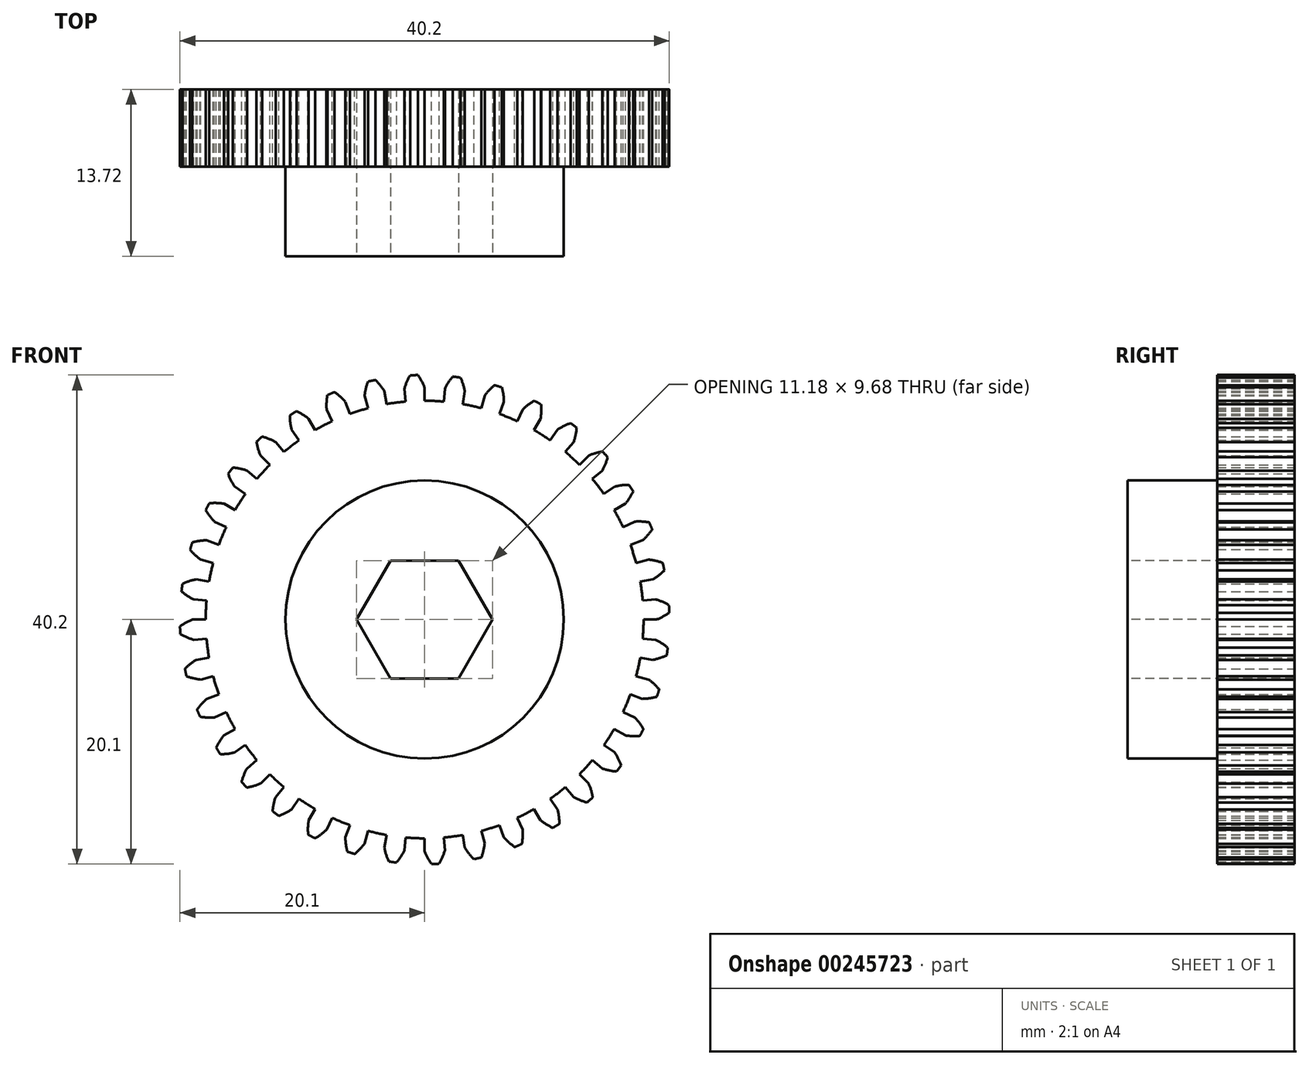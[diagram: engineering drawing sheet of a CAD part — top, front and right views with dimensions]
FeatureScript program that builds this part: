
annotation { "Feature Type Name" : "Feature", "Feature Type Description" : "" }
export const myFeature = defineFeature(function(context is Context, id is Id, definition is map)
    precondition{}
    {
        {
            var Q0;
            Q0=qCreatedBy(makeId("Front.planeOp"),FACE);
            var sketch = newSketch(context, id + "F0", { "sketchPlane" : qUnion([Q0])});
            skArc(sketch, "E0", {"start": v(4.65, 17.37) * mm, "mid": v(-6.88, -16.61) * mm, "end": v(9, 15.57) * mm});
            skLineSegment(sketch, "E1", {"start": v(0, 17.98) * mm, "end": v(0, 19.05) * mm});
            skLineSegment(sketch, "E2", {"start": v(0, 0) * mm, "end": v(-0.88, 20.08) * mm, "construction": true});
            skArc(sketch, "E3.trimOffspring", {"start": v(-0.56, 20.1) * mm, "mid": v(-0.72, 20.1) * mm, "end": v(-0.88, 20.08) * mm});
            skArc(sketch, "E4.trimOffspring", {"start": v(0, 19.05) * mm, "mid": v(-0.25, 19.6) * mm, "end": v(-0.56, 20.1) * mm});
            skLineSegment(sketch, "E5.MirrorCS", {"start": v(-1.57, 17.91) * mm, "end": v(-1.66, 18.98) * mm});
            skArc(sketch, "E6.MirrorCS", {"start": v(-1.66, 18.98) * mm, "mid": v(-1.46, 19.54) * mm, "end": v(-1.2, 20.07) * mm});
            skArc(sketch, "E7.MirrorCS", {"start": v(-1.2, 20.07) * mm, "mid": v(-1.03, 20.08) * mm, "end": v(-0.88, 20.08) * mm});
            skLineSegment(sketch, "E8.1.0", {"start": v(-4.65, 17.37) * mm, "end": v(-4.93, 18.4) * mm});
            skArc(sketch, "E8.1.1", {"start": v(-3.3, 18.76) * mm, "mid": v(-3.65, 19.25) * mm, "end": v(-4.04, 19.7) * mm});
            skLineSegment(sketch, "E8.1.2", {"start": v(-3.12, 17.7) * mm, "end": v(-3.3, 18.76) * mm});
            skArc(sketch, "E8.1.3", {"start": v(-4.93, 18.4) * mm, "mid": v(-4.83, 18.99) * mm, "end": v(-4.66, 19.56) * mm});
            skArc(sketch, "E8.1.4", {"start": v(-4.66, 19.56) * mm, "mid": v(-4.5, 19.6) * mm, "end": v(-4.35, 19.63) * mm});
            skArc(sketch, "E8.1.5", {"start": v(-4.04, 19.7) * mm, "mid": v(-4.2, 19.66) * mm, "end": v(-4.35, 19.63) * mm});
            skLineSegment(sketch, "E8.2.0", {"start": v(-7.6, 16.3) * mm, "end": v(-8.05, 17.27) * mm});
            skArc(sketch, "E8.2.1", {"start": v(-6.52, 17.9) * mm, "mid": v(-6.93, 18.32) * mm, "end": v(-7.4, 18.7) * mm});
            skLineSegment(sketch, "E8.2.2", {"start": v(-6.15, 16.9) * mm, "end": v(-6.52, 17.9) * mm});
            skArc(sketch, "E8.2.3", {"start": v(-8.05, 17.27) * mm, "mid": v(-8.05, 17.86) * mm, "end": v(-7.98, 18.45) * mm});
            skArc(sketch, "E8.2.4", {"start": v(-7.98, 18.45) * mm, "mid": v(-7.84, 18.51) * mm, "end": v(-7.7, 18.57) * mm});
            skArc(sketch, "E8.2.5", {"start": v(-7.4, 18.7) * mm, "mid": v(-7.55, 18.63) * mm, "end": v(-7.7, 18.57) * mm});
            skLineSegment(sketch, "E8.3.0", {"start": v(-10.31, 14.73) * mm, "end": v(-10.93, 15.6) * mm});
            skArc(sketch, "E8.3.1", {"start": v(-9.52, 16.5) * mm, "mid": v(-10, 16.84) * mm, "end": v(-10.53, 17.12) * mm});
            skLineSegment(sketch, "E8.3.2", {"start": v(-9, 15.57) * mm, "end": v(-9.52, 16.5) * mm});
            skArc(sketch, "E8.3.3", {"start": v(-10.93, 15.6) * mm, "mid": v(-11.03, 16.19) * mm, "end": v(-11.07, 16.78) * mm});
            skArc(sketch, "E8.3.4", {"start": v(-11.07, 16.78) * mm, "mid": v(-10.93, 16.87) * mm, "end": v(-10.8, 16.96) * mm});
            skArc(sketch, "E8.3.5", {"start": v(-10.53, 17.12) * mm, "mid": v(-10.67, 17.04) * mm, "end": v(-10.8, 16.96) * mm});
            skLineSegment(sketch, "E8.4.0", {"start": v(-12.72, 12.72) * mm, "end": v(-13.47, 13.47) * mm});
            skArc(sketch, "E8.4.1", {"start": v(-12.25, 14.6) * mm, "mid": v(-12.78, 14.85) * mm, "end": v(-13.35, 15.03) * mm});
            skLineSegment(sketch, "E8.4.2", {"start": v(-11.56, 13.78) * mm, "end": v(-12.25, 14.6) * mm});
            skArc(sketch, "E8.4.3", {"start": v(-13.47, 13.47) * mm, "mid": v(-13.68, 14.03) * mm, "end": v(-13.81, 14.6) * mm});
            skArc(sketch, "E8.4.4", {"start": v(-13.81, 14.6) * mm, "mid": v(-13.7, 14.72) * mm, "end": v(-13.58, 14.82) * mm});
            skArc(sketch, "E8.4.5", {"start": v(-13.35, 15.03) * mm, "mid": v(-13.47, 14.93) * mm, "end": v(-13.58, 14.82) * mm});
            skLineSegment(sketch, "E8.5.0", {"start": v(-14.73, 10.31) * mm, "end": v(-15.6, 10.93) * mm});
            skArc(sketch, "E8.5.1", {"start": v(-14.6, 12.25) * mm, "mid": v(-15.17, 12.4) * mm, "end": v(-15.76, 12.49) * mm});
            skLineSegment(sketch, "E8.5.2", {"start": v(-13.78, 11.56) * mm, "end": v(-14.6, 12.25) * mm});
            skArc(sketch, "E8.5.3", {"start": v(-15.6, 10.93) * mm, "mid": v(-15.9, 11.44) * mm, "end": v(-16.14, 11.99) * mm});
            skArc(sketch, "E8.5.4", {"start": v(-16.14, 11.99) * mm, "mid": v(-16.05, 12.11) * mm, "end": v(-15.95, 12.24) * mm});
            skArc(sketch, "E8.5.5", {"start": v(-15.76, 12.49) * mm, "mid": v(-15.85, 12.36) * mm, "end": v(-15.95, 12.24) * mm});
            skLineSegment(sketch, "E8.6.0", {"start": v(-16.3, 7.6) * mm, "end": v(-17.27, 8.05) * mm});
            skArc(sketch, "E8.6.1", {"start": v(-16.5, 9.53) * mm, "mid": v(-17.09, 9.58) * mm, "end": v(-17.68, 9.56) * mm});
            skLineSegment(sketch, "E8.6.2", {"start": v(-15.57, 9) * mm, "end": v(-16.5, 9.53) * mm});
            skArc(sketch, "E8.6.3", {"start": v(-17.27, 8.05) * mm, "mid": v(-17.65, 8.5) * mm, "end": v(-17.98, 9) * mm});
            skArc(sketch, "E8.6.4", {"start": v(-17.98, 9) * mm, "mid": v(-17.9, 9.14) * mm, "end": v(-17.83, 9.28) * mm});
            skArc(sketch, "E8.6.5", {"start": v(-17.68, 9.56) * mm, "mid": v(-17.76, 9.42) * mm, "end": v(-17.83, 9.28) * mm});
            skLineSegment(sketch, "E8.7.0", {"start": v(-17.37, 4.65) * mm, "end": v(-18.4, 4.93) * mm});
            skArc(sketch, "E8.7.1", {"start": v(-17.9, 6.52) * mm, "mid": v(-18.5, 6.47) * mm, "end": v(-19.08, 6.35) * mm});
            skLineSegment(sketch, "E8.7.2", {"start": v(-16.9, 6.15) * mm, "end": v(-17.9, 6.52) * mm});
            skArc(sketch, "E8.7.3", {"start": v(-18.4, 4.93) * mm, "mid": v(-18.86, 5.3) * mm, "end": v(-19.27, 5.74) * mm});
            skArc(sketch, "E8.7.4", {"start": v(-19.27, 5.74) * mm, "mid": v(-19.22, 5.9) * mm, "end": v(-19.17, 6.05) * mm});
            skArc(sketch, "E8.7.5", {"start": v(-19.08, 6.35) * mm, "mid": v(-19.13, 6.2) * mm, "end": v(-19.17, 6.05) * mm});
            skLineSegment(sketch, "E8.8.0", {"start": v(-17.91, 1.57) * mm, "end": v(-18.98, 1.66) * mm});
            skArc(sketch, "E8.8.1", {"start": v(-18.76, 3.3) * mm, "mid": v(-19.34, 3.16) * mm, "end": v(-19.89, 2.94) * mm});
            skLineSegment(sketch, "E8.8.2", {"start": v(-17.7, 3.12) * mm, "end": v(-18.76, 3.3) * mm});
            skArc(sketch, "E8.8.3", {"start": v(-18.98, 1.66) * mm, "mid": v(-19.5, 1.95) * mm, "end": v(-19.97, 2.31) * mm});
            skArc(sketch, "E8.8.4", {"start": v(-19.97, 2.31) * mm, "mid": v(-19.95, 2.47) * mm, "end": v(-19.93, 2.62) * mm});
            skArc(sketch, "E8.8.5", {"start": v(-19.89, 2.94) * mm, "mid": v(-19.91, 2.78) * mm, "end": v(-19.93, 2.62) * mm});
            skLineSegment(sketch, "E8.9.0", {"start": v(-17.91, -1.57) * mm, "end": v(-18.98, -1.66) * mm});
            skArc(sketch, "E8.9.1", {"start": v(-19.05, 0) * mm, "mid": v(-19.6, -0.25) * mm, "end": v(-20.1, -0.56) * mm});
            skLineSegment(sketch, "E8.9.2", {"start": v(-17.98, 0) * mm, "end": v(-19.05, 0) * mm});
            skArc(sketch, "E8.9.3", {"start": v(-18.98, -1.66) * mm, "mid": v(-19.54, -1.46) * mm, "end": v(-20.07, -1.2) * mm});
            skArc(sketch, "E8.9.4", {"start": v(-20.07, -1.2) * mm, "mid": v(-20.08, -1.03) * mm, "end": v(-20.08, -0.88) * mm});
            skArc(sketch, "E8.9.5", {"start": v(-20.1, -0.56) * mm, "mid": v(-20.1, -0.72) * mm, "end": v(-20.08, -0.88) * mm});
            skLineSegment(sketch, "E8.10.0", {"start": v(-17.37, -4.65) * mm, "end": v(-18.4, -4.93) * mm});
            skArc(sketch, "E8.10.1", {"start": v(-18.76, -3.3) * mm, "mid": v(-19.25, -3.65) * mm, "end": v(-19.7, -4.04) * mm});
            skLineSegment(sketch, "E8.10.2", {"start": v(-17.7, -3.12) * mm, "end": v(-18.76, -3.3) * mm});
            skArc(sketch, "E8.10.3", {"start": v(-18.4, -4.93) * mm, "mid": v(-18.99, -4.83) * mm, "end": v(-19.56, -4.66) * mm});
            skArc(sketch, "E8.10.4", {"start": v(-19.56, -4.66) * mm, "mid": v(-19.6, -4.5) * mm, "end": v(-19.63, -4.35) * mm});
            skArc(sketch, "E8.10.5", {"start": v(-19.7, -4.04) * mm, "mid": v(-19.66, -4.2) * mm, "end": v(-19.63, -4.35) * mm});
            skLineSegment(sketch, "E8.11.0", {"start": v(-16.3, -7.6) * mm, "end": v(-17.27, -8.05) * mm});
            skArc(sketch, "E8.11.1", {"start": v(-17.9, -6.52) * mm, "mid": v(-18.32, -6.93) * mm, "end": v(-18.7, -7.4) * mm});
            skLineSegment(sketch, "E8.11.2", {"start": v(-16.9, -6.15) * mm, "end": v(-17.9, -6.52) * mm});
            skArc(sketch, "E8.11.3", {"start": v(-17.27, -8.05) * mm, "mid": v(-17.86, -8.05) * mm, "end": v(-18.45, -7.98) * mm});
            skArc(sketch, "E8.11.4", {"start": v(-18.45, -7.98) * mm, "mid": v(-18.51, -7.84) * mm, "end": v(-18.57, -7.7) * mm});
            skArc(sketch, "E8.11.5", {"start": v(-18.7, -7.4) * mm, "mid": v(-18.63, -7.55) * mm, "end": v(-18.57, -7.7) * mm});
            skLineSegment(sketch, "E8.12.0", {"start": v(-14.73, -10.31) * mm, "end": v(-15.6, -10.93) * mm});
            skArc(sketch, "E8.12.1", {"start": v(-16.5, -9.52) * mm, "mid": v(-16.84, -10) * mm, "end": v(-17.12, -10.53) * mm});
            skLineSegment(sketch, "E8.12.2", {"start": v(-15.57, -9) * mm, "end": v(-16.5, -9.52) * mm});
            skArc(sketch, "E8.12.3", {"start": v(-15.6, -10.93) * mm, "mid": v(-16.19, -11.03) * mm, "end": v(-16.78, -11.07) * mm});
            skArc(sketch, "E8.12.4", {"start": v(-16.78, -11.07) * mm, "mid": v(-16.87, -10.93) * mm, "end": v(-16.96, -10.8) * mm});
            skArc(sketch, "E8.12.5", {"start": v(-17.12, -10.53) * mm, "mid": v(-17.04, -10.67) * mm, "end": v(-16.96, -10.8) * mm});
            skLineSegment(sketch, "E8.13.0", {"start": v(-12.72, -12.72) * mm, "end": v(-13.47, -13.47) * mm});
            skArc(sketch, "E8.13.1", {"start": v(-14.6, -12.25) * mm, "mid": v(-14.85, -12.78) * mm, "end": v(-15.03, -13.35) * mm});
            skLineSegment(sketch, "E8.13.2", {"start": v(-13.78, -11.56) * mm, "end": v(-14.6, -12.25) * mm});
            skArc(sketch, "E8.13.3", {"start": v(-13.47, -13.47) * mm, "mid": v(-14.03, -13.68) * mm, "end": v(-14.6, -13.81) * mm});
            skArc(sketch, "E8.13.4", {"start": v(-14.6, -13.81) * mm, "mid": v(-14.72, -13.7) * mm, "end": v(-14.82, -13.58) * mm});
            skArc(sketch, "E8.13.5", {"start": v(-15.03, -13.35) * mm, "mid": v(-14.93, -13.47) * mm, "end": v(-14.82, -13.58) * mm});
            skLineSegment(sketch, "E8.14.0", {"start": v(-10.31, -14.73) * mm, "end": v(-10.93, -15.6) * mm});
            skArc(sketch, "E8.14.1", {"start": v(-12.25, -14.6) * mm, "mid": v(-12.4, -15.17) * mm, "end": v(-12.49, -15.76) * mm});
            skLineSegment(sketch, "E8.14.2", {"start": v(-11.56, -13.78) * mm, "end": v(-12.25, -14.6) * mm});
            skArc(sketch, "E8.14.3", {"start": v(-10.93, -15.6) * mm, "mid": v(-11.44, -15.9) * mm, "end": v(-11.99, -16.14) * mm});
            skArc(sketch, "E8.14.4", {"start": v(-11.99, -16.14) * mm, "mid": v(-12.11, -16.05) * mm, "end": v(-12.24, -15.95) * mm});
            skArc(sketch, "E8.14.5", {"start": v(-12.49, -15.76) * mm, "mid": v(-12.36, -15.85) * mm, "end": v(-12.24, -15.95) * mm});
            skLineSegment(sketch, "E8.15.0", {"start": v(-7.6, -16.3) * mm, "end": v(-8.05, -17.27) * mm});
            skArc(sketch, "E8.15.1", {"start": v(-9.53, -16.5) * mm, "mid": v(-9.58, -17.09) * mm, "end": v(-9.56, -17.68) * mm});
            skLineSegment(sketch, "E8.15.2", {"start": v(-9, -15.57) * mm, "end": v(-9.53, -16.5) * mm});
            skArc(sketch, "E8.15.3", {"start": v(-8.05, -17.27) * mm, "mid": v(-8.5, -17.65) * mm, "end": v(-9, -17.98) * mm});
            skArc(sketch, "E8.15.4", {"start": v(-9, -17.98) * mm, "mid": v(-9.14, -17.9) * mm, "end": v(-9.28, -17.83) * mm});
            skArc(sketch, "E8.15.5", {"start": v(-9.56, -17.68) * mm, "mid": v(-9.42, -17.76) * mm, "end": v(-9.28, -17.83) * mm});
            skLineSegment(sketch, "E8.16.0", {"start": v(-4.65, -17.37) * mm, "end": v(-4.93, -18.4) * mm});
            skArc(sketch, "E8.16.1", {"start": v(-6.52, -17.9) * mm, "mid": v(-6.47, -18.5) * mm, "end": v(-6.35, -19.08) * mm});
            skLineSegment(sketch, "E8.16.2", {"start": v(-6.15, -16.9) * mm, "end": v(-6.52, -17.9) * mm});
            skArc(sketch, "E8.16.3", {"start": v(-4.93, -18.4) * mm, "mid": v(-5.3, -18.86) * mm, "end": v(-5.74, -19.27) * mm});
            skArc(sketch, "E8.16.4", {"start": v(-5.74, -19.27) * mm, "mid": v(-5.9, -19.22) * mm, "end": v(-6.05, -19.17) * mm});
            skArc(sketch, "E8.16.5", {"start": v(-6.35, -19.08) * mm, "mid": v(-6.2, -19.13) * mm, "end": v(-6.05, -19.17) * mm});
            skLineSegment(sketch, "E8.17.0", {"start": v(-1.57, -17.91) * mm, "end": v(-1.66, -18.98) * mm});
            skArc(sketch, "E8.17.1", {"start": v(-3.3, -18.76) * mm, "mid": v(-3.16, -19.34) * mm, "end": v(-2.94, -19.89) * mm});
            skLineSegment(sketch, "E8.17.2", {"start": v(-3.12, -17.7) * mm, "end": v(-3.3, -18.76) * mm});
            skArc(sketch, "E8.17.3", {"start": v(-1.66, -18.98) * mm, "mid": v(-1.95, -19.5) * mm, "end": v(-2.31, -19.97) * mm});
            skArc(sketch, "E8.17.4", {"start": v(-2.31, -19.97) * mm, "mid": v(-2.47, -19.95) * mm, "end": v(-2.62, -19.93) * mm});
            skArc(sketch, "E8.17.5", {"start": v(-2.94, -19.89) * mm, "mid": v(-2.78, -19.91) * mm, "end": v(-2.62, -19.93) * mm});
            skLineSegment(sketch, "E8.18.0", {"start": v(1.57, -17.91) * mm, "end": v(1.66, -18.98) * mm});
            skArc(sketch, "E8.18.1", {"start": v(0, -19.05) * mm, "mid": v(0.25, -19.6) * mm, "end": v(0.56, -20.1) * mm});
            skLineSegment(sketch, "E8.18.2", {"start": v(0, -17.98) * mm, "end": v(0, -19.05) * mm});
            skArc(sketch, "E8.18.3", {"start": v(1.66, -18.98) * mm, "mid": v(1.46, -19.54) * mm, "end": v(1.2, -20.07) * mm});
            skArc(sketch, "E8.18.4", {"start": v(1.2, -20.07) * mm, "mid": v(1.03, -20.08) * mm, "end": v(0.88, -20.08) * mm});
            skArc(sketch, "E8.18.5", {"start": v(0.56, -20.1) * mm, "mid": v(0.72, -20.1) * mm, "end": v(0.88, -20.08) * mm});
            skLineSegment(sketch, "E8.19.0", {"start": v(4.65, -17.37) * mm, "end": v(4.93, -18.4) * mm});
            skArc(sketch, "E8.19.1", {"start": v(3.3, -18.76) * mm, "mid": v(3.65, -19.25) * mm, "end": v(4.04, -19.7) * mm});
            skLineSegment(sketch, "E8.19.2", {"start": v(3.12, -17.7) * mm, "end": v(3.3, -18.76) * mm});
            skArc(sketch, "E8.19.3", {"start": v(4.93, -18.4) * mm, "mid": v(4.83, -18.99) * mm, "end": v(4.66, -19.56) * mm});
            skArc(sketch, "E8.19.4", {"start": v(4.66, -19.56) * mm, "mid": v(4.5, -19.6) * mm, "end": v(4.35, -19.63) * mm});
            skArc(sketch, "E8.19.5", {"start": v(4.04, -19.7) * mm, "mid": v(4.2, -19.66) * mm, "end": v(4.35, -19.63) * mm});
            skLineSegment(sketch, "E8.20.0", {"start": v(7.6, -16.3) * mm, "end": v(8.05, -17.27) * mm});
            skArc(sketch, "E8.20.1", {"start": v(6.52, -17.9) * mm, "mid": v(6.93, -18.32) * mm, "end": v(7.4, -18.7) * mm});
            skLineSegment(sketch, "E8.20.2", {"start": v(6.15, -16.9) * mm, "end": v(6.52, -17.9) * mm});
            skArc(sketch, "E8.20.3", {"start": v(8.05, -17.27) * mm, "mid": v(8.05, -17.86) * mm, "end": v(7.98, -18.45) * mm});
            skArc(sketch, "E8.20.4", {"start": v(7.98, -18.45) * mm, "mid": v(7.84, -18.51) * mm, "end": v(7.7, -18.57) * mm});
            skArc(sketch, "E8.20.5", {"start": v(7.4, -18.7) * mm, "mid": v(7.55, -18.63) * mm, "end": v(7.7, -18.57) * mm});
            skLineSegment(sketch, "E8.21.0", {"start": v(10.31, -14.73) * mm, "end": v(10.93, -15.6) * mm});
            skArc(sketch, "E8.21.1", {"start": v(9.52, -16.5) * mm, "mid": v(10, -16.84) * mm, "end": v(10.53, -17.12) * mm});
            skLineSegment(sketch, "E8.21.2", {"start": v(9, -15.57) * mm, "end": v(9.53, -16.5) * mm});
            skArc(sketch, "E8.21.3", {"start": v(10.93, -15.6) * mm, "mid": v(11.03, -16.19) * mm, "end": v(11.07, -16.78) * mm});
            skArc(sketch, "E8.21.4", {"start": v(11.07, -16.78) * mm, "mid": v(10.93, -16.87) * mm, "end": v(10.8, -16.96) * mm});
            skArc(sketch, "E8.21.5", {"start": v(10.53, -17.12) * mm, "mid": v(10.67, -17.04) * mm, "end": v(10.8, -16.96) * mm});
            skLineSegment(sketch, "E8.22.0", {"start": v(12.72, -12.72) * mm, "end": v(13.47, -13.47) * mm});
            skArc(sketch, "E8.22.1", {"start": v(12.25, -14.6) * mm, "mid": v(12.78, -14.85) * mm, "end": v(13.35, -15.03) * mm});
            skLineSegment(sketch, "E8.22.2", {"start": v(11.56, -13.78) * mm, "end": v(12.25, -14.6) * mm});
            skArc(sketch, "E8.22.3", {"start": v(13.47, -13.47) * mm, "mid": v(13.68, -14.03) * mm, "end": v(13.81, -14.6) * mm});
            skArc(sketch, "E8.22.4", {"start": v(13.81, -14.6) * mm, "mid": v(13.7, -14.72) * mm, "end": v(13.58, -14.82) * mm});
            skArc(sketch, "E8.22.5", {"start": v(13.35, -15.03) * mm, "mid": v(13.47, -14.93) * mm, "end": v(13.58, -14.82) * mm});
            skLineSegment(sketch, "E8.23.0", {"start": v(14.73, -10.31) * mm, "end": v(15.6, -10.93) * mm});
            skArc(sketch, "E8.23.1", {"start": v(14.6, -12.25) * mm, "mid": v(15.17, -12.4) * mm, "end": v(15.76, -12.49) * mm});
            skLineSegment(sketch, "E8.23.2", {"start": v(13.78, -11.56) * mm, "end": v(14.6, -12.25) * mm});
            skArc(sketch, "E8.23.3", {"start": v(15.6, -10.93) * mm, "mid": v(15.9, -11.44) * mm, "end": v(16.14, -11.99) * mm});
            skArc(sketch, "E8.23.4", {"start": v(16.14, -11.99) * mm, "mid": v(16.05, -12.11) * mm, "end": v(15.95, -12.24) * mm});
            skArc(sketch, "E8.23.5", {"start": v(15.76, -12.49) * mm, "mid": v(15.85, -12.36) * mm, "end": v(15.95, -12.24) * mm});
            skLineSegment(sketch, "E8.24.0", {"start": v(16.3, -7.6) * mm, "end": v(17.27, -8.05) * mm});
            skArc(sketch, "E8.24.1", {"start": v(16.5, -9.53) * mm, "mid": v(17.09, -9.58) * mm, "end": v(17.68, -9.56) * mm});
            skLineSegment(sketch, "E8.24.2", {"start": v(15.57, -9) * mm, "end": v(16.5, -9.53) * mm});
            skArc(sketch, "E8.24.3", {"start": v(17.27, -8.05) * mm, "mid": v(17.65, -8.5) * mm, "end": v(17.98, -9) * mm});
            skArc(sketch, "E8.24.4", {"start": v(17.98, -9) * mm, "mid": v(17.9, -9.14) * mm, "end": v(17.83, -9.28) * mm});
            skArc(sketch, "E8.24.5", {"start": v(17.68, -9.56) * mm, "mid": v(17.76, -9.42) * mm, "end": v(17.83, -9.28) * mm});
            skLineSegment(sketch, "E8.25.0", {"start": v(17.37, -4.65) * mm, "end": v(18.4, -4.93) * mm});
            skArc(sketch, "E8.25.1", {"start": v(17.9, -6.52) * mm, "mid": v(18.5, -6.47) * mm, "end": v(19.08, -6.35) * mm});
            skLineSegment(sketch, "E8.25.2", {"start": v(16.9, -6.15) * mm, "end": v(17.9, -6.52) * mm});
            skArc(sketch, "E8.25.3", {"start": v(18.4, -4.93) * mm, "mid": v(18.86, -5.3) * mm, "end": v(19.27, -5.74) * mm});
            skArc(sketch, "E8.25.4", {"start": v(19.27, -5.74) * mm, "mid": v(19.22, -5.9) * mm, "end": v(19.17, -6.05) * mm});
            skArc(sketch, "E8.25.5", {"start": v(19.08, -6.35) * mm, "mid": v(19.13, -6.2) * mm, "end": v(19.17, -6.05) * mm});
            skLineSegment(sketch, "E8.26.0", {"start": v(17.91, -1.57) * mm, "end": v(18.98, -1.66) * mm});
            skArc(sketch, "E8.26.1", {"start": v(18.76, -3.3) * mm, "mid": v(19.34, -3.16) * mm, "end": v(19.89, -2.94) * mm});
            skLineSegment(sketch, "E8.26.2", {"start": v(17.7, -3.12) * mm, "end": v(18.76, -3.3) * mm});
            skArc(sketch, "E8.26.3", {"start": v(18.98, -1.66) * mm, "mid": v(19.5, -1.95) * mm, "end": v(19.97, -2.31) * mm});
            skArc(sketch, "E8.26.4", {"start": v(19.97, -2.31) * mm, "mid": v(19.95, -2.47) * mm, "end": v(19.93, -2.62) * mm});
            skArc(sketch, "E8.26.5", {"start": v(19.89, -2.94) * mm, "mid": v(19.91, -2.78) * mm, "end": v(19.93, -2.62) * mm});
            skLineSegment(sketch, "E8.27.0", {"start": v(17.91, 1.57) * mm, "end": v(18.98, 1.66) * mm});
            skArc(sketch, "E8.27.1", {"start": v(19.05, 0) * mm, "mid": v(19.6, 0.25) * mm, "end": v(20.1, 0.56) * mm});
            skLineSegment(sketch, "E8.27.2", {"start": v(17.98, 0) * mm, "end": v(19.05, 0) * mm});
            skArc(sketch, "E8.27.3", {"start": v(18.98, 1.66) * mm, "mid": v(19.54, 1.46) * mm, "end": v(20.07, 1.2) * mm});
            skArc(sketch, "E8.27.4", {"start": v(20.07, 1.2) * mm, "mid": v(20.08, 1.03) * mm, "end": v(20.08, 0.88) * mm});
            skArc(sketch, "E8.27.5", {"start": v(20.1, 0.56) * mm, "mid": v(20.1, 0.72) * mm, "end": v(20.08, 0.88) * mm});
            skLineSegment(sketch, "E8.28.0", {"start": v(17.37, 4.65) * mm, "end": v(18.4, 4.93) * mm});
            skArc(sketch, "E8.28.1", {"start": v(18.76, 3.3) * mm, "mid": v(19.25, 3.65) * mm, "end": v(19.7, 4.04) * mm});
            skLineSegment(sketch, "E8.28.2", {"start": v(17.7, 3.12) * mm, "end": v(18.76, 3.3) * mm});
            skArc(sketch, "E8.28.3", {"start": v(18.4, 4.93) * mm, "mid": v(18.99, 4.83) * mm, "end": v(19.56, 4.66) * mm});
            skArc(sketch, "E8.28.4", {"start": v(19.56, 4.66) * mm, "mid": v(19.6, 4.5) * mm, "end": v(19.63, 4.35) * mm});
            skArc(sketch, "E8.28.5", {"start": v(19.7, 4.04) * mm, "mid": v(19.66, 4.2) * mm, "end": v(19.63, 4.35) * mm});
            skLineSegment(sketch, "E8.29.0", {"start": v(16.3, 7.6) * mm, "end": v(17.27, 8.05) * mm});
            skArc(sketch, "E8.29.1", {"start": v(17.9, 6.52) * mm, "mid": v(18.32, 6.93) * mm, "end": v(18.7, 7.4) * mm});
            skLineSegment(sketch, "E8.29.2", {"start": v(16.9, 6.15) * mm, "end": v(17.9, 6.52) * mm});
            skArc(sketch, "E8.29.3", {"start": v(17.27, 8.05) * mm, "mid": v(17.86, 8.05) * mm, "end": v(18.45, 7.98) * mm});
            skArc(sketch, "E8.29.4", {"start": v(18.45, 7.98) * mm, "mid": v(18.51, 7.84) * mm, "end": v(18.57, 7.7) * mm});
            skArc(sketch, "E8.29.5", {"start": v(18.7, 7.4) * mm, "mid": v(18.63, 7.55) * mm, "end": v(18.57, 7.7) * mm});
            skLineSegment(sketch, "E8.30.0", {"start": v(14.73, 10.31) * mm, "end": v(15.6, 10.93) * mm});
            skArc(sketch, "E8.30.1", {"start": v(16.5, 9.52) * mm, "mid": v(16.84, 10) * mm, "end": v(17.12, 10.53) * mm});
            skLineSegment(sketch, "E8.30.2", {"start": v(15.57, 9) * mm, "end": v(16.5, 9.52) * mm});
            skArc(sketch, "E8.30.3", {"start": v(15.6, 10.93) * mm, "mid": v(16.19, 11.03) * mm, "end": v(16.78, 11.07) * mm});
            skArc(sketch, "E8.30.4", {"start": v(16.78, 11.07) * mm, "mid": v(16.87, 10.93) * mm, "end": v(16.96, 10.8) * mm});
            skArc(sketch, "E8.30.5", {"start": v(17.12, 10.53) * mm, "mid": v(17.04, 10.67) * mm, "end": v(16.96, 10.8) * mm});
            skLineSegment(sketch, "E8.31.0", {"start": v(12.72, 12.72) * mm, "end": v(13.47, 13.47) * mm});
            skArc(sketch, "E8.31.1", {"start": v(14.6, 12.25) * mm, "mid": v(14.85, 12.78) * mm, "end": v(15.03, 13.35) * mm});
            skLineSegment(sketch, "E8.31.2", {"start": v(13.78, 11.56) * mm, "end": v(14.6, 12.25) * mm});
            skArc(sketch, "E8.31.3", {"start": v(13.47, 13.47) * mm, "mid": v(14.03, 13.68) * mm, "end": v(14.6, 13.81) * mm});
            skArc(sketch, "E8.31.4", {"start": v(14.6, 13.81) * mm, "mid": v(14.72, 13.7) * mm, "end": v(14.82, 13.58) * mm});
            skArc(sketch, "E8.31.5", {"start": v(15.03, 13.35) * mm, "mid": v(14.93, 13.47) * mm, "end": v(14.82, 13.58) * mm});
            skLineSegment(sketch, "E8.32.0", {"start": v(10.31, 14.73) * mm, "end": v(10.93, 15.6) * mm});
            skArc(sketch, "E8.32.1", {"start": v(12.25, 14.6) * mm, "mid": v(12.4, 15.17) * mm, "end": v(12.49, 15.76) * mm});
            skLineSegment(sketch, "E8.32.2", {"start": v(11.56, 13.78) * mm, "end": v(12.25, 14.6) * mm});
            skArc(sketch, "E8.32.3", {"start": v(10.93, 15.6) * mm, "mid": v(11.44, 15.9) * mm, "end": v(11.99, 16.14) * mm});
            skArc(sketch, "E8.32.4", {"start": v(11.99, 16.14) * mm, "mid": v(12.11, 16.05) * mm, "end": v(12.24, 15.95) * mm});
            skArc(sketch, "E8.32.5", {"start": v(12.49, 15.76) * mm, "mid": v(12.36, 15.85) * mm, "end": v(12.24, 15.95) * mm});
            skLineSegment(sketch, "E8.33.0", {"start": v(7.6, 16.3) * mm, "end": v(8.05, 17.27) * mm});
            skArc(sketch, "E8.33.1", {"start": v(9.53, 16.5) * mm, "mid": v(9.58, 17.09) * mm, "end": v(9.56, 17.68) * mm});
            skLineSegment(sketch, "E8.33.2", {"start": v(9, 15.57) * mm, "end": v(9.52, 16.5) * mm});
            skArc(sketch, "E8.33.3", {"start": v(8.05, 17.27) * mm, "mid": v(8.5, 17.65) * mm, "end": v(9, 17.98) * mm});
            skArc(sketch, "E8.33.4", {"start": v(9, 17.98) * mm, "mid": v(9.14, 17.9) * mm, "end": v(9.28, 17.83) * mm});
            skArc(sketch, "E8.33.5", {"start": v(9.56, 17.68) * mm, "mid": v(9.42, 17.76) * mm, "end": v(9.28, 17.83) * mm});
            skLineSegment(sketch, "E8.34.0", {"start": v(4.65, 17.37) * mm, "end": v(4.93, 18.4) * mm});
            skArc(sketch, "E8.34.1", {"start": v(6.52, 17.9) * mm, "mid": v(6.47, 18.5) * mm, "end": v(6.35, 19.08) * mm});
            skLineSegment(sketch, "E8.34.2", {"start": v(6.15, 16.9) * mm, "end": v(6.52, 17.9) * mm});
            skArc(sketch, "E8.34.3", {"start": v(4.93, 18.4) * mm, "mid": v(5.3, 18.86) * mm, "end": v(5.74, 19.27) * mm});
            skArc(sketch, "E8.34.4", {"start": v(5.74, 19.27) * mm, "mid": v(5.9, 19.22) * mm, "end": v(6.05, 19.17) * mm});
            skArc(sketch, "E8.34.5", {"start": v(6.35, 19.08) * mm, "mid": v(6.2, 19.13) * mm, "end": v(6.05, 19.17) * mm});
            skLineSegment(sketch, "E8.35.0", {"start": v(1.57, 17.91) * mm, "end": v(1.66, 18.98) * mm});
            skArc(sketch, "E8.35.1", {"start": v(3.3, 18.76) * mm, "mid": v(3.16, 19.34) * mm, "end": v(2.94, 19.89) * mm});
            skLineSegment(sketch, "E8.35.2", {"start": v(3.12, 17.7) * mm, "end": v(3.3, 18.76) * mm});
            skArc(sketch, "E8.35.3", {"start": v(1.66, 18.98) * mm, "mid": v(1.95, 19.5) * mm, "end": v(2.31, 19.97) * mm});
            skArc(sketch, "E8.35.4", {"start": v(2.31, 19.97) * mm, "mid": v(2.47, 19.95) * mm, "end": v(2.62, 19.93) * mm});
            skArc(sketch, "E8.35.5", {"start": v(2.94, 19.89) * mm, "mid": v(2.78, 19.91) * mm, "end": v(2.62, 19.93) * mm});
            skArc(sketch, "E9.trimOffspring", {"start": v(7.6, 16.3) * mm, "mid": v(6.88, 16.61) * mm, "end": v(6.15, 16.9) * mm});
            skSolve(sketch);
        }
        {
            var Q0;
            Q0=makeQuery(id+"F0.imprint","IMPRINT",FACE,{"disambiguationData":[TD([[makeQuery(id+"F0.imprint","IMPRINT",EDGE,{"derivedFrom":sQuery(id+"F0.wireOp",EDGE,"E8.33.0")}),-1.0]])]});
            var Q1;
            {var subQ1=sQuery(id+"F0.wireOp",EDGE,"E8.3.0");Q1=makeQuery(id+"F0.imprint","IMPRINT",FACE,{"disambiguationData":[TD([[makeQuery(id+"F0.imprint","IMPRINT",EDGE,{"derivedFrom":subQ1}),-1.0]])]});}
            var Q2;
            {var subQ1=sQuery(id+"F0.wireOp",EDGE,"E8.11.0");Q2=makeQuery(id+"F0.imprint","IMPRINT",FACE,{"disambiguationData":[TD([[makeQuery(id+"F0.imprint","IMPRINT",EDGE,{"derivedFrom":subQ1}),-1.0]])]});}
            var Q3;
            {var subQ1=sQuery(id+"F0.wireOp",EDGE,"E8.20.0");Q3=makeQuery(id+"F0.imprint","IMPRINT",FACE,{"disambiguationData":[TD([[makeQuery(id+"F0.imprint","IMPRINT",EDGE,{"derivedFrom":subQ1}),-1.0]])]});}
            var Q4;
            {var subQ1=sQuery(id+"F0.wireOp",EDGE,"E8.14.0");Q4=makeQuery(id+"F0.imprint","IMPRINT",FACE,{"disambiguationData":[TD([[makeQuery(id+"F0.imprint","IMPRINT",EDGE,{"derivedFrom":subQ1}),-1.0]])]});}
            var Q5;
            {var subQ1=sQuery(id+"F0.wireOp",EDGE,"E8.13.0");Q5=makeQuery(id+"F0.imprint","IMPRINT",FACE,{"disambiguationData":[TD([[makeQuery(id+"F0.imprint","IMPRINT",EDGE,{"derivedFrom":subQ1}),-1.0]])]});}
            var Q6;
            {var subQ1=sQuery(id+"F0.wireOp",EDGE,"E8.2.0");Q6=makeQuery(id+"F0.imprint","IMPRINT",FACE,{"disambiguationData":[TD([[makeQuery(id+"F0.imprint","IMPRINT",EDGE,{"derivedFrom":subQ1}),-1.0]])]});}
            var Q7;
            {var subQ0=sQuery(id+"F0.wireOp",EDGE,"E8.4.0");Q7=makeQuery(id+"F0.imprint","IMPRINT",FACE,{"disambiguationData":[TD([[makeQuery(id+"F0.imprint","IMPRINT",EDGE,{"derivedFrom":subQ0}),-1.0]])]});}
            var Q8;
            {var subQ1=sQuery(id+"F0.wireOp",EDGE,"E8.6.0");Q8=makeQuery(id+"F0.imprint","IMPRINT",FACE,{"disambiguationData":[TD([[makeQuery(id+"F0.imprint","IMPRINT",EDGE,{"derivedFrom":subQ1}),-1.0]])]});}
            var Q9;
            {var subQ1=sQuery(id+"F0.wireOp",EDGE,"E8.30.0");Q9=makeQuery(id+"F0.imprint","IMPRINT",FACE,{"disambiguationData":[TD([[makeQuery(id+"F0.imprint","IMPRINT",EDGE,{"derivedFrom":subQ1}),-1.0]])]});}
            var Q10;
            {var subQ1=sQuery(id+"F0.wireOp",EDGE,"E8.22.0");Q10=makeQuery(id+"F0.imprint","IMPRINT",FACE,{"disambiguationData":[TD([[makeQuery(id+"F0.imprint","IMPRINT",EDGE,{"derivedFrom":subQ1}),-1.0]])]});}
            var Q11;
            {var subQ0=sQuery(id+"F0.wireOp",EDGE,"E8.23.0");Q11=makeQuery(id+"F0.imprint","IMPRINT",FACE,{"disambiguationData":[TD([[makeQuery(id+"F0.imprint","IMPRINT",EDGE,{"derivedFrom":subQ0}),-1.0]])]});}
            var Q12;
            {var subQ1=sQuery(id+"F0.wireOp",EDGE,"E8.28.0");Q12=makeQuery(id+"F0.imprint","IMPRINT",FACE,{"disambiguationData":[TD([[makeQuery(id+"F0.imprint","IMPRINT",EDGE,{"derivedFrom":subQ1}),-1.0]])]});}
            var Q13;
            {var subQ1=sQuery(id+"F0.wireOp",EDGE,"E8.29.0");Q13=makeQuery(id+"F0.imprint","IMPRINT",FACE,{"disambiguationData":[TD([[makeQuery(id+"F0.imprint","IMPRINT",EDGE,{"derivedFrom":subQ1}),-1.0]])]});}
            var Q14;
            {var subQ0=sQuery(id+"F0.wireOp",EDGE,"E8.15.0");Q14=makeQuery(id+"F0.imprint","IMPRINT",FACE,{"disambiguationData":[TD([[makeQuery(id+"F0.imprint","IMPRINT",EDGE,{"derivedFrom":subQ0}),-1.0]])]});}
            var Q15;
            {var subQ1=sQuery(id+"F0.wireOp",EDGE,"E8.31.0");Q15=makeQuery(id+"F0.imprint","IMPRINT",FACE,{"disambiguationData":[TD([[makeQuery(id+"F0.imprint","IMPRINT",EDGE,{"derivedFrom":subQ1}),-1.0]])]});}
            var Q16;
            {var subQ1=sQuery(id+"F0.wireOp",EDGE,"E8.16.0");Q16=makeQuery(id+"F0.imprint","IMPRINT",FACE,{"disambiguationData":[TD([[makeQuery(id+"F0.imprint","IMPRINT",EDGE,{"derivedFrom":subQ1}),-1.0]])]});}
            var Q17;
            {var subQ1=sQuery(id+"F0.wireOp",EDGE,"E8.32.0");Q17=makeQuery(id+"F0.imprint","IMPRINT",FACE,{"disambiguationData":[TD([[makeQuery(id+"F0.imprint","IMPRINT",EDGE,{"derivedFrom":subQ1}),-1.0]])]});}
            var Q18;
            {var subQ1=sQuery(id+"F0.wireOp",EDGE,"E8.17.0");Q18=makeQuery(id+"F0.imprint","IMPRINT",FACE,{"disambiguationData":[TD([[makeQuery(id+"F0.imprint","IMPRINT",EDGE,{"derivedFrom":subQ1}),-1.0]])]});}
            var Q19;
            {var subQ1=sQuery(id+"F0.wireOp",EDGE,"E8.18.0");Q19=makeQuery(id+"F0.imprint","IMPRINT",FACE,{"disambiguationData":[TD([[makeQuery(id+"F0.imprint","IMPRINT",EDGE,{"derivedFrom":subQ1}),-1.0]])]});}
            var Q20;
            {var subQ0=sQuery(id+"F0.wireOp",EDGE,"E8.19.0");Q20=makeQuery(id+"F0.imprint","IMPRINT",FACE,{"disambiguationData":[TD([[makeQuery(id+"F0.imprint","IMPRINT",EDGE,{"derivedFrom":subQ0}),-1.0]])]});}
            var Q21;
            {var subQ0=sQuery(id+"F0.wireOp",EDGE,"E8.21.0");Q21=makeQuery(id+"F0.imprint","IMPRINT",FACE,{"disambiguationData":[TD([[makeQuery(id+"F0.imprint","IMPRINT",EDGE,{"derivedFrom":subQ0}),-1.0]])]});}
            var Q22;
            {var subQ1=sQuery(id+"F0.wireOp",EDGE,"E8.12.0");Q22=makeQuery(id+"F0.imprint","IMPRINT",FACE,{"disambiguationData":[TD([[makeQuery(id+"F0.imprint","IMPRINT",EDGE,{"derivedFrom":subQ1}),-1.0]])]});}
            var Q23;
            {var subQ1=sQuery(id+"F0.wireOp",EDGE,"E8.35.0");Q23=makeQuery(id+"F0.imprint","IMPRINT",FACE,{"disambiguationData":[TD([[makeQuery(id+"F0.imprint","IMPRINT",EDGE,{"derivedFrom":subQ1}),-1.0]])]});}
            var Q24;
            {var subQ0=sQuery(id+"F0.wireOp",EDGE,"E1");Q24=makeQuery(id+"F0.imprint","IMPRINT",FACE,{"disambiguationData":[TD([[makeQuery(id+"F0.imprint","IMPRINT",EDGE,{"derivedFrom":subQ0}),1.0]])]});}
            var Q25;
            {var subQ1=sQuery(id+"F0.wireOp",EDGE,"E8.1.0");Q25=makeQuery(id+"F0.imprint","IMPRINT",FACE,{"disambiguationData":[TD([[makeQuery(id+"F0.imprint","IMPRINT",EDGE,{"derivedFrom":subQ1}),-1.0]])]});}
            var Q26;
            {var subQ1=sQuery(id+"F0.wireOp",EDGE,"E8.5.0");Q26=makeQuery(id+"F0.imprint","IMPRINT",FACE,{"disambiguationData":[TD([[makeQuery(id+"F0.imprint","IMPRINT",EDGE,{"derivedFrom":subQ1}),-1.0]])]});}
            var Q27;
            {var subQ1=sQuery(id+"F0.wireOp",EDGE,"E8.7.0");Q27=makeQuery(id+"F0.imprint","IMPRINT",FACE,{"disambiguationData":[TD([[makeQuery(id+"F0.imprint","IMPRINT",EDGE,{"derivedFrom":subQ1}),-1.0]])]});}
            var Q28;
            {var subQ1=sQuery(id+"F0.wireOp",EDGE,"E8.8.0");Q28=makeQuery(id+"F0.imprint","IMPRINT",FACE,{"disambiguationData":[TD([[makeQuery(id+"F0.imprint","IMPRINT",EDGE,{"derivedFrom":subQ1}),-1.0]])]});}
            var Q29;
            {var subQ1=sQuery(id+"F0.wireOp",EDGE,"E8.25.0");Q29=makeQuery(id+"F0.imprint","IMPRINT",FACE,{"disambiguationData":[TD([[makeQuery(id+"F0.imprint","IMPRINT",EDGE,{"derivedFrom":subQ1}),-1.0]])]});}
            var Q30;
            {var subQ1=sQuery(id+"F0.wireOp",EDGE,"E8.9.0");Q30=makeQuery(id+"F0.imprint","IMPRINT",FACE,{"disambiguationData":[TD([[makeQuery(id+"F0.imprint","IMPRINT",EDGE,{"derivedFrom":subQ1}),-1.0]])]});}
            var Q31;
            {var subQ1=sQuery(id+"F0.wireOp",EDGE,"E8.10.0");Q31=makeQuery(id+"F0.imprint","IMPRINT",FACE,{"disambiguationData":[TD([[makeQuery(id+"F0.imprint","IMPRINT",EDGE,{"derivedFrom":subQ1}),-1.0]])]});}
            var Q32;
            {var subQ1=sQuery(id+"F0.wireOp",EDGE,"E8.27.0");Q32=makeQuery(id+"F0.imprint","IMPRINT",FACE,{"disambiguationData":[TD([[makeQuery(id+"F0.imprint","IMPRINT",EDGE,{"derivedFrom":subQ1}),-1.0]])]});}
            var Q33;
            {var subQ1=sQuery(id+"F0.wireOp",EDGE,"E8.26.0");Q33=makeQuery(id+"F0.imprint","IMPRINT",FACE,{"disambiguationData":[TD([[makeQuery(id+"F0.imprint","IMPRINT",EDGE,{"derivedFrom":subQ1}),-1.0]])]});}
            var Q34;
            {var subQ1=sQuery(id+"F0.wireOp",EDGE,"E8.24.0");Q34=makeQuery(id+"F0.imprint","IMPRINT",FACE,{"disambiguationData":[TD([[makeQuery(id+"F0.imprint","IMPRINT",EDGE,{"derivedFrom":subQ1}),-1.0]])]});}
            extrude(context, id + "F1", {"entities" : qUnion([Q0, Q1, Q2, Q3, Q4, Q5, Q6, Q7, Q8, Q9, Q10, Q11, Q12, Q13, Q14, Q15, Q16, Q17, Q18, Q19, Q20, Q21, Q22, Q23, Q24, Q25, Q26, Q27, Q28, Q29, Q30, Q31, Q32, Q33, Q34]), "depth" : 6.35 * mm});
        }
        {
            var Q0;
            Q0=makeQuery(id+"F1.opExtrude","CAP_FACE",FACE,{"disambiguationData":[OSD([sQuery(id+"F0.wireOp",EDGE,"E0"),sQuery(id+"F0.wireOp",EDGE,"E1"),sQuery(id+"F0.wireOp",EDGE,"E3.trimOffspring"),sQuery(id+"F0.wireOp",EDGE,"E4.trimOffspring"),sQuery(id+"F0.wireOp",EDGE,"E5.MirrorCS"),sQuery(id+"F0.wireOp",EDGE,"E6.MirrorCS"),sQuery(id+"F0.wireOp",EDGE,"E7.MirrorCS"),sQuery(id+"F0.wireOp",EDGE,"E8.1.0"),sQuery(id+"F0.wireOp",EDGE,"E8.1.1"),sQuery(id+"F0.wireOp",EDGE,"E8.1.2"),sQuery(id+"F0.wireOp",EDGE,"E8.1.3"),sQuery(id+"F0.wireOp",EDGE,"E8.1.4"),sQuery(id+"F0.wireOp",EDGE,"E8.1.5"),sQuery(id+"F0.wireOp",EDGE,"E8.2.0"),sQuery(id+"F0.wireOp",EDGE,"E8.2.1"),sQuery(id+"F0.wireOp",EDGE,"E8.2.2"),sQuery(id+"F0.wireOp",EDGE,"E8.2.3"),sQuery(id+"F0.wireOp",EDGE,"E8.2.4"),sQuery(id+"F0.wireOp",EDGE,"E8.2.5"),sQuery(id+"F0.wireOp",EDGE,"E8.3.0"),sQuery(id+"F0.wireOp",EDGE,"E8.3.1"),sQuery(id+"F0.wireOp",EDGE,"E8.3.2"),sQuery(id+"F0.wireOp",EDGE,"E8.3.3"),sQuery(id+"F0.wireOp",EDGE,"E8.3.4"),sQuery(id+"F0.wireOp",EDGE,"E8.3.5"),sQuery(id+"F0.wireOp",EDGE,"E8.4.0"),sQuery(id+"F0.wireOp",EDGE,"E8.4.1"),sQuery(id+"F0.wireOp",EDGE,"E8.4.2"),sQuery(id+"F0.wireOp",EDGE,"E8.4.3"),sQuery(id+"F0.wireOp",EDGE,"E8.4.4"),sQuery(id+"F0.wireOp",EDGE,"E8.4.5"),sQuery(id+"F0.wireOp",EDGE,"E8.5.0"),sQuery(id+"F0.wireOp",EDGE,"E8.5.1"),sQuery(id+"F0.wireOp",EDGE,"E8.5.2"),sQuery(id+"F0.wireOp",EDGE,"E8.5.3"),sQuery(id+"F0.wireOp",EDGE,"E8.5.4"),sQuery(id+"F0.wireOp",EDGE,"E8.5.5"),sQuery(id+"F0.wireOp",EDGE,"E8.6.0"),sQuery(id+"F0.wireOp",EDGE,"E8.6.1"),sQuery(id+"F0.wireOp",EDGE,"E8.6.2"),sQuery(id+"F0.wireOp",EDGE,"E8.6.3"),sQuery(id+"F0.wireOp",EDGE,"E8.6.4"),sQuery(id+"F0.wireOp",EDGE,"E8.6.5"),sQuery(id+"F0.wireOp",EDGE,"E8.7.0"),sQuery(id+"F0.wireOp",EDGE,"E8.7.1"),sQuery(id+"F0.wireOp",EDGE,"E8.7.2"),sQuery(id+"F0.wireOp",EDGE,"E8.7.3"),sQuery(id+"F0.wireOp",EDGE,"E8.7.4"),sQuery(id+"F0.wireOp",EDGE,"E8.7.5"),sQuery(id+"F0.wireOp",EDGE,"E8.8.0"),sQuery(id+"F0.wireOp",EDGE,"E8.8.1"),sQuery(id+"F0.wireOp",EDGE,"E8.8.2"),sQuery(id+"F0.wireOp",EDGE,"E8.8.3"),sQuery(id+"F0.wireOp",EDGE,"E8.8.4"),sQuery(id+"F0.wireOp",EDGE,"E8.8.5"),sQuery(id+"F0.wireOp",EDGE,"E8.9.0"),sQuery(id+"F0.wireOp",EDGE,"E8.9.1"),sQuery(id+"F0.wireOp",EDGE,"E8.9.2"),sQuery(id+"F0.wireOp",EDGE,"E8.9.3"),sQuery(id+"F0.wireOp",EDGE,"E8.9.4"),sQuery(id+"F0.wireOp",EDGE,"E8.9.5"),sQuery(id+"F0.wireOp",EDGE,"E8.10.0"),sQuery(id+"F0.wireOp",EDGE,"E8.10.1"),sQuery(id+"F0.wireOp",EDGE,"E8.10.2"),sQuery(id+"F0.wireOp",EDGE,"E8.10.3"),sQuery(id+"F0.wireOp",EDGE,"E8.10.4"),sQuery(id+"F0.wireOp",EDGE,"E8.10.5"),sQuery(id+"F0.wireOp",EDGE,"E8.11.0"),sQuery(id+"F0.wireOp",EDGE,"E8.11.1"),sQuery(id+"F0.wireOp",EDGE,"E8.11.2"),sQuery(id+"F0.wireOp",EDGE,"E8.11.3"),sQuery(id+"F0.wireOp",EDGE,"E8.11.4"),sQuery(id+"F0.wireOp",EDGE,"E8.11.5"),sQuery(id+"F0.wireOp",EDGE,"E8.12.0"),sQuery(id+"F0.wireOp",EDGE,"E8.12.1"),sQuery(id+"F0.wireOp",EDGE,"E8.12.2"),sQuery(id+"F0.wireOp",EDGE,"E8.12.3"),sQuery(id+"F0.wireOp",EDGE,"E8.12.4"),sQuery(id+"F0.wireOp",EDGE,"E8.12.5"),sQuery(id+"F0.wireOp",EDGE,"E8.13.0"),sQuery(id+"F0.wireOp",EDGE,"E8.13.1"),sQuery(id+"F0.wireOp",EDGE,"E8.13.2"),sQuery(id+"F0.wireOp",EDGE,"E8.13.3"),sQuery(id+"F0.wireOp",EDGE,"E8.13.4"),sQuery(id+"F0.wireOp",EDGE,"E8.13.5"),sQuery(id+"F0.wireOp",EDGE,"E8.14.0"),sQuery(id+"F0.wireOp",EDGE,"E8.14.1"),sQuery(id+"F0.wireOp",EDGE,"E8.14.2"),sQuery(id+"F0.wireOp",EDGE,"E8.14.3"),sQuery(id+"F0.wireOp",EDGE,"E8.14.4"),sQuery(id+"F0.wireOp",EDGE,"E8.14.5"),sQuery(id+"F0.wireOp",EDGE,"E8.15.0"),sQuery(id+"F0.wireOp",EDGE,"E8.15.1"),sQuery(id+"F0.wireOp",EDGE,"E8.15.2"),sQuery(id+"F0.wireOp",EDGE,"E8.15.3"),sQuery(id+"F0.wireOp",EDGE,"E8.15.4"),sQuery(id+"F0.wireOp",EDGE,"E8.15.5"),sQuery(id+"F0.wireOp",EDGE,"E8.16.0"),sQuery(id+"F0.wireOp",EDGE,"E8.16.1"),sQuery(id+"F0.wireOp",EDGE,"E8.16.2"),sQuery(id+"F0.wireOp",EDGE,"E8.16.3"),sQuery(id+"F0.wireOp",EDGE,"E8.16.4"),sQuery(id+"F0.wireOp",EDGE,"E8.16.5"),sQuery(id+"F0.wireOp",EDGE,"E8.17.0"),sQuery(id+"F0.wireOp",EDGE,"E8.17.1"),sQuery(id+"F0.wireOp",EDGE,"E8.17.2"),sQuery(id+"F0.wireOp",EDGE,"E8.17.3"),sQuery(id+"F0.wireOp",EDGE,"E8.17.4"),sQuery(id+"F0.wireOp",EDGE,"E8.17.5"),sQuery(id+"F0.wireOp",EDGE,"E8.18.0"),sQuery(id+"F0.wireOp",EDGE,"E8.18.1"),sQuery(id+"F0.wireOp",EDGE,"E8.18.2"),sQuery(id+"F0.wireOp",EDGE,"E8.18.3"),sQuery(id+"F0.wireOp",EDGE,"E8.18.4"),sQuery(id+"F0.wireOp",EDGE,"E8.18.5"),sQuery(id+"F0.wireOp",EDGE,"E8.19.0"),sQuery(id+"F0.wireOp",EDGE,"E8.19.1"),sQuery(id+"F0.wireOp",EDGE,"E8.19.2"),sQuery(id+"F0.wireOp",EDGE,"E8.19.3"),sQuery(id+"F0.wireOp",EDGE,"E8.19.4"),sQuery(id+"F0.wireOp",EDGE,"E8.19.5"),sQuery(id+"F0.wireOp",EDGE,"E8.20.0"),sQuery(id+"F0.wireOp",EDGE,"E8.20.1"),sQuery(id+"F0.wireOp",EDGE,"E8.20.2"),sQuery(id+"F0.wireOp",EDGE,"E8.20.3"),sQuery(id+"F0.wireOp",EDGE,"E8.20.4"),sQuery(id+"F0.wireOp",EDGE,"E8.20.5"),sQuery(id+"F0.wireOp",EDGE,"E8.21.0"),sQuery(id+"F0.wireOp",EDGE,"E8.21.1"),sQuery(id+"F0.wireOp",EDGE,"E8.21.2"),sQuery(id+"F0.wireOp",EDGE,"E8.21.3"),sQuery(id+"F0.wireOp",EDGE,"E8.21.4"),sQuery(id+"F0.wireOp",EDGE,"E8.21.5"),sQuery(id+"F0.wireOp",EDGE,"E8.22.0"),sQuery(id+"F0.wireOp",EDGE,"E8.22.1"),sQuery(id+"F0.wireOp",EDGE,"E8.22.2"),sQuery(id+"F0.wireOp",EDGE,"E8.22.3"),sQuery(id+"F0.wireOp",EDGE,"E8.22.4"),sQuery(id+"F0.wireOp",EDGE,"E8.22.5"),sQuery(id+"F0.wireOp",EDGE,"E8.23.0"),sQuery(id+"F0.wireOp",EDGE,"E8.23.1"),sQuery(id+"F0.wireOp",EDGE,"E8.23.2"),sQuery(id+"F0.wireOp",EDGE,"E8.23.3"),sQuery(id+"F0.wireOp",EDGE,"E8.23.4"),sQuery(id+"F0.wireOp",EDGE,"E8.23.5"),sQuery(id+"F0.wireOp",EDGE,"E8.24.0"),sQuery(id+"F0.wireOp",EDGE,"E8.24.1"),sQuery(id+"F0.wireOp",EDGE,"E8.24.2"),sQuery(id+"F0.wireOp",EDGE,"E8.24.3"),sQuery(id+"F0.wireOp",EDGE,"E8.24.4"),sQuery(id+"F0.wireOp",EDGE,"E8.24.5"),sQuery(id+"F0.wireOp",EDGE,"E8.25.0"),sQuery(id+"F0.wireOp",EDGE,"E8.25.1"),sQuery(id+"F0.wireOp",EDGE,"E8.25.2"),sQuery(id+"F0.wireOp",EDGE,"E8.25.3"),sQuery(id+"F0.wireOp",EDGE,"E8.25.4"),sQuery(id+"F0.wireOp",EDGE,"E8.25.5"),sQuery(id+"F0.wireOp",EDGE,"E8.26.0"),sQuery(id+"F0.wireOp",EDGE,"E8.26.1"),sQuery(id+"F0.wireOp",EDGE,"E8.26.2"),sQuery(id+"F0.wireOp",EDGE,"E8.26.3"),sQuery(id+"F0.wireOp",EDGE,"E8.26.4"),sQuery(id+"F0.wireOp",EDGE,"E8.26.5"),sQuery(id+"F0.wireOp",EDGE,"E8.27.0"),sQuery(id+"F0.wireOp",EDGE,"E8.27.1"),sQuery(id+"F0.wireOp",EDGE,"E8.27.2"),sQuery(id+"F0.wireOp",EDGE,"E8.27.3"),sQuery(id+"F0.wireOp",EDGE,"E8.27.4"),sQuery(id+"F0.wireOp",EDGE,"E8.27.5"),sQuery(id+"F0.wireOp",EDGE,"E8.28.0"),sQuery(id+"F0.wireOp",EDGE,"E8.28.1"),sQuery(id+"F0.wireOp",EDGE,"E8.28.2"),sQuery(id+"F0.wireOp",EDGE,"E8.28.3"),sQuery(id+"F0.wireOp",EDGE,"E8.28.4"),sQuery(id+"F0.wireOp",EDGE,"E8.28.5"),sQuery(id+"F0.wireOp",EDGE,"E8.29.0"),sQuery(id+"F0.wireOp",EDGE,"E8.29.1"),sQuery(id+"F0.wireOp",EDGE,"E8.29.2"),sQuery(id+"F0.wireOp",EDGE,"E8.29.3"),sQuery(id+"F0.wireOp",EDGE,"E8.29.4"),sQuery(id+"F0.wireOp",EDGE,"E8.29.5"),sQuery(id+"F0.wireOp",EDGE,"E8.30.0"),sQuery(id+"F0.wireOp",EDGE,"E8.30.1"),sQuery(id+"F0.wireOp",EDGE,"E8.30.2"),sQuery(id+"F0.wireOp",EDGE,"E8.30.3"),sQuery(id+"F0.wireOp",EDGE,"E8.30.4"),sQuery(id+"F0.wireOp",EDGE,"E8.30.5"),sQuery(id+"F0.wireOp",EDGE,"E8.31.0"),sQuery(id+"F0.wireOp",EDGE,"E8.31.1"),sQuery(id+"F0.wireOp",EDGE,"E8.31.2"),sQuery(id+"F0.wireOp",EDGE,"E8.31.3"),sQuery(id+"F0.wireOp",EDGE,"E8.31.4"),sQuery(id+"F0.wireOp",EDGE,"E8.31.5"),sQuery(id+"F0.wireOp",EDGE,"E8.32.0"),sQuery(id+"F0.wireOp",EDGE,"E8.32.1"),sQuery(id+"F0.wireOp",EDGE,"E8.32.2"),sQuery(id+"F0.wireOp",EDGE,"E8.32.3"),sQuery(id+"F0.wireOp",EDGE,"E8.32.4"),sQuery(id+"F0.wireOp",EDGE,"E8.32.5"),sQuery(id+"F0.wireOp",EDGE,"E8.33.0"),sQuery(id+"F0.wireOp",EDGE,"E8.33.1"),sQuery(id+"F0.wireOp",EDGE,"E8.33.2"),sQuery(id+"F0.wireOp",EDGE,"E8.33.3"),sQuery(id+"F0.wireOp",EDGE,"E8.33.4"),sQuery(id+"F0.wireOp",EDGE,"E8.33.5"),sQuery(id+"F0.wireOp",EDGE,"E8.34.0"),sQuery(id+"F0.wireOp",EDGE,"E8.34.1"),sQuery(id+"F0.wireOp",EDGE,"E8.34.2"),sQuery(id+"F0.wireOp",EDGE,"E8.34.3"),sQuery(id+"F0.wireOp",EDGE,"E8.34.4"),sQuery(id+"F0.wireOp",EDGE,"E8.34.5"),sQuery(id+"F0.wireOp",EDGE,"E8.35.0"),sQuery(id+"F0.wireOp",EDGE,"E8.35.1"),sQuery(id+"F0.wireOp",EDGE,"E8.35.2"),sQuery(id+"F0.wireOp",EDGE,"E8.35.3"),sQuery(id+"F0.wireOp",EDGE,"E8.35.4"),sQuery(id+"F0.wireOp",EDGE,"E8.35.5"),sQuery(id+"F0.wireOp",EDGE,"E9.trimOffspring")])],"isStart":false});
            var sketch = newSketch(context, id + "F2", { "sketchPlane" : qUnion([Q0])});
            skCircle(sketch, "E10", {"center": v(0, 0) * mm, "radius": 11.43 * mm});
            skSolve(sketch);
        }
        {
            var Q0;
            Q0 = qSketchRegion(id + "F2", true);
            extrude(context, id + "F3", {"entities" : qUnion([Q0]), "operationType" : NewBodyOperationType.ADD, "depth" : 7.37 * mm});
        }
        {
            var Q0;
            Q0=makeQuery(id+"F3.opExtrude","CAP_FACE",FACE,{"disambiguationData":[OSD([sQuery(id+"F2.wireOp",EDGE,"E10")])],"isStart":false});
            var sketch = newSketch(context, id + "F4", { "sketchPlane" : qUnion([Q0])});
            skCircle(sketch, "E11.cCircle", {"center": v(0, 0) * mm, "radius": 5.59 * mm, "construction": true});
            skLineSegment(sketch, "E11.0", {"start": v(5.59, 0) * mm, "end": v(2.8, -4.84) * mm});
            skLineSegment(sketch, "E11.1", {"start": v(2.8, -4.84) * mm, "end": v(-2.8, -4.84) * mm});
            skLineSegment(sketch, "E11.2", {"start": v(-2.8, -4.84) * mm, "end": v(-5.59, 0) * mm});
            skLineSegment(sketch, "E11.3", {"start": v(-5.59, 0) * mm, "end": v(-2.8, 4.84) * mm});
            skLineSegment(sketch, "E11.4", {"start": v(-2.8, 4.84) * mm, "end": v(2.8, 4.84) * mm});
            skLineSegment(sketch, "E11.5", {"start": v(2.8, 4.84) * mm, "end": v(5.59, 0) * mm});
            skSolve(sketch);
        }
        {
            var Q0;
            Q0=makeQuery(id+"F4.imprint","IMPRINT",FACE,{"disambiguationData":[TD([[makeQuery(id+"F4.imprint","IMPRINT",EDGE,{"derivedFrom":sQuery(id+"F4.wireOp",EDGE,"E11.0")}),-1.0]])]});
            extrude(context, id + "F5", {"entities" : qUnion([Q0]), "operationType" : NewBodyOperationType.REMOVE, "oppositeDirection" : true, "depth" : 25.4 * mm});
        }
    });
